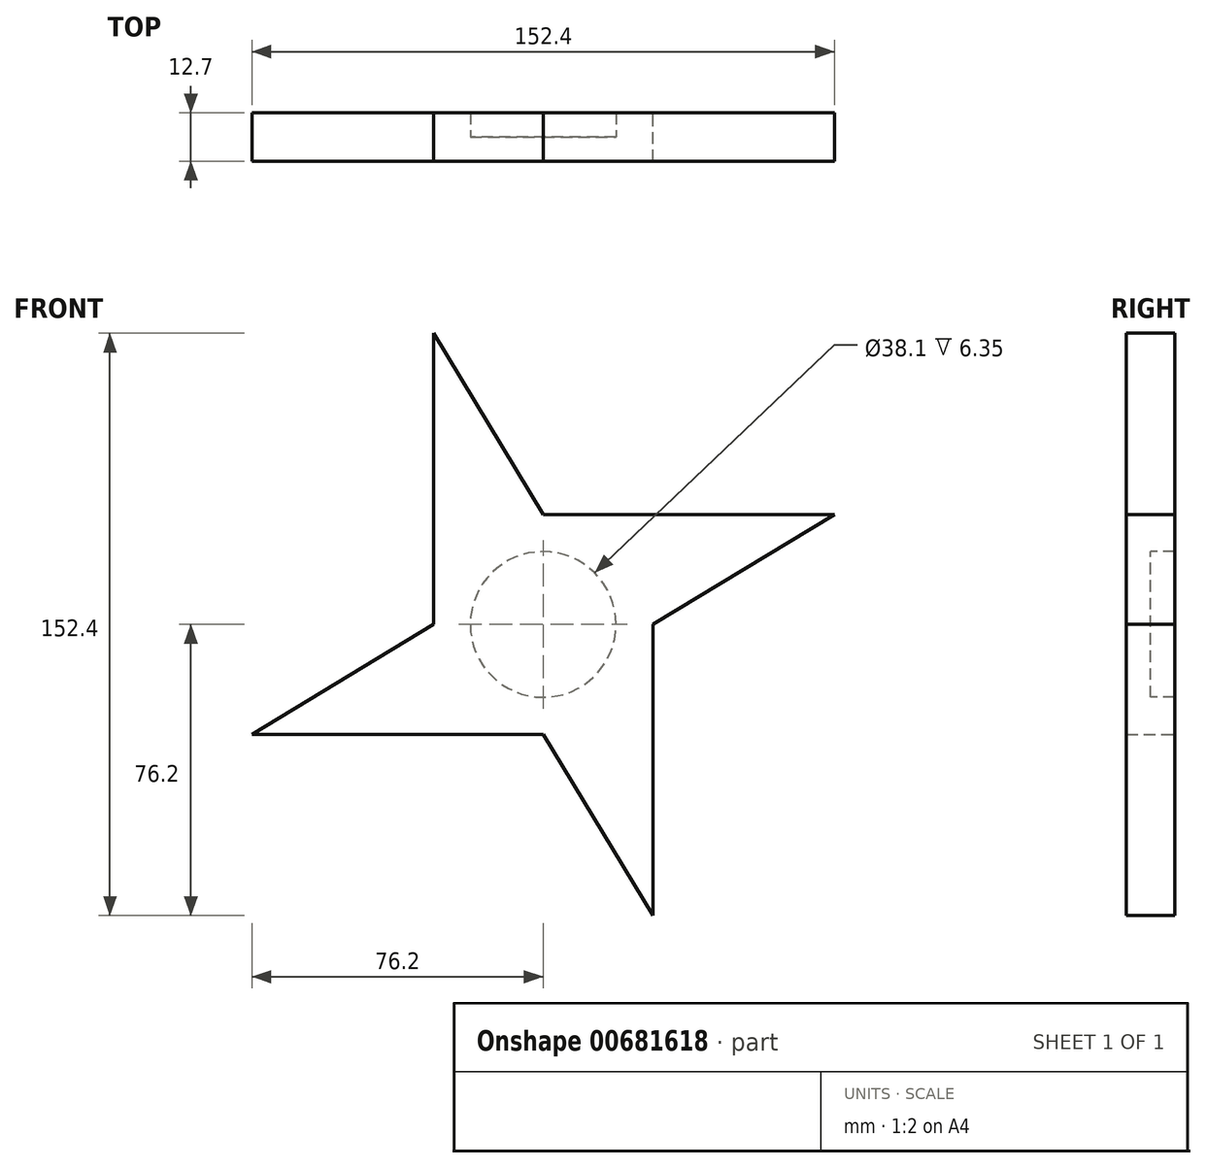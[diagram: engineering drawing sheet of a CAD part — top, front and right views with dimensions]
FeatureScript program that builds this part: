
annotation { "Feature Type Name" : "Feature", "Feature Type Description" : "" }
export const myFeature = defineFeature(function(context is Context, id is Id, definition is map)
    precondition{}
    {
        {
            var Q0;
            Q0=qCreatedBy(makeId("Front.planeOp"),FACE);
            var sketch = newSketch(context, id + "F0", { "sketchPlane" : qUnion([Q0])});
            skCircle(sketch, "E0", {"center": v(0, 0) * mm, "radius": 28.72 * mm});
            skLineSegment(sketch, "E1", {"start": v(28.72, 0) * mm, "end": v(-28.72, 0) * mm});
            skLineSegment(sketch, "E2", {"start": v(-28.72, 0) * mm, "end": v(-28.72, 76.2) * mm});
            skLineSegment(sketch, "E3", {"start": v(-28.72, 76.2) * mm, "end": v(0, 28.72) * mm});
            skLineSegment(sketch, "E4", {"start": v(0, 28.72) * mm, "end": v(76.2, 28.72) * mm});
            skLineSegment(sketch, "E5", {"start": v(76.2, 28.72) * mm, "end": v(28.72, 0) * mm});
            skLineSegment(sketch, "E6", {"start": v(28.72, 0) * mm, "end": v(28.72, -76.2) * mm});
            skLineSegment(sketch, "E7", {"start": v(28.72, -76.2) * mm, "end": v(0, -28.72) * mm});
            skLineSegment(sketch, "E8", {"start": v(0, -28.72) * mm, "end": v(-76.2, -28.72) * mm});
            skLineSegment(sketch, "E9", {"start": v(-76.2, -28.72) * mm, "end": v(-28.72, 0) * mm});
            skSolve(sketch);
        }
        {
            var Q0;
            Q0 = qSketchRegion(id + "F0", true);
            extrude(context, id + "F1", {"entities" : qUnion([Q0]), "endBound" : BoundingType.SYMMETRIC, "depth" : 12.7 * mm, "offsetDistance" : 25.4 * mm});
        }
        {
            var Q0;
            Q0=qCreatedBy(makeId("Front.planeOp"),FACE);
            var sketch = newSketch(context, id + "F2", { "sketchPlane" : qUnion([Q0])});
            skCircle(sketch, "E10", {"center": v(0, 0) * mm, "radius": 18.4 * mm});
            skSolve(sketch);
        }
        {
            var Q0;
            Q0=sQuery(id+"F2.wireOp",VERTEX,"E10.center");
            var Q1;
            Q1=makeQuery(id+"F1.opExtrude","SWEPT_BODY",BODY,{"disambiguationData":[OSD([sQuery(id+"F0.wireOp",EDGE,"E2"),sQuery(id+"F0.wireOp",EDGE,"E3"),sQuery(id+"F0.wireOp",EDGE,"E4"),sQuery(id+"F0.wireOp",EDGE,"E5"),sQuery(id+"F0.wireOp",EDGE,"E6"),sQuery(id+"F0.wireOp",EDGE,"E7"),sQuery(id+"F0.wireOp",EDGE,"E8"),sQuery(id+"F0.wireOp",EDGE,"E9")])]});
            hole(context, id + "F3", {"style" : HoleStyle.SIMPLE, "endStyle" : HoleEndStyle.THROUGH, "holeDiameter" : 38.1 * mm, "majorDiameter" : 6.35 * mm, "isTappedThrough" : true, "tappedDepth" : 12.7 * mm, "tapClearance" : 3, "locations" : qUnion([Q0]), "scope" : qUnion([Q1])});
        }
    });
